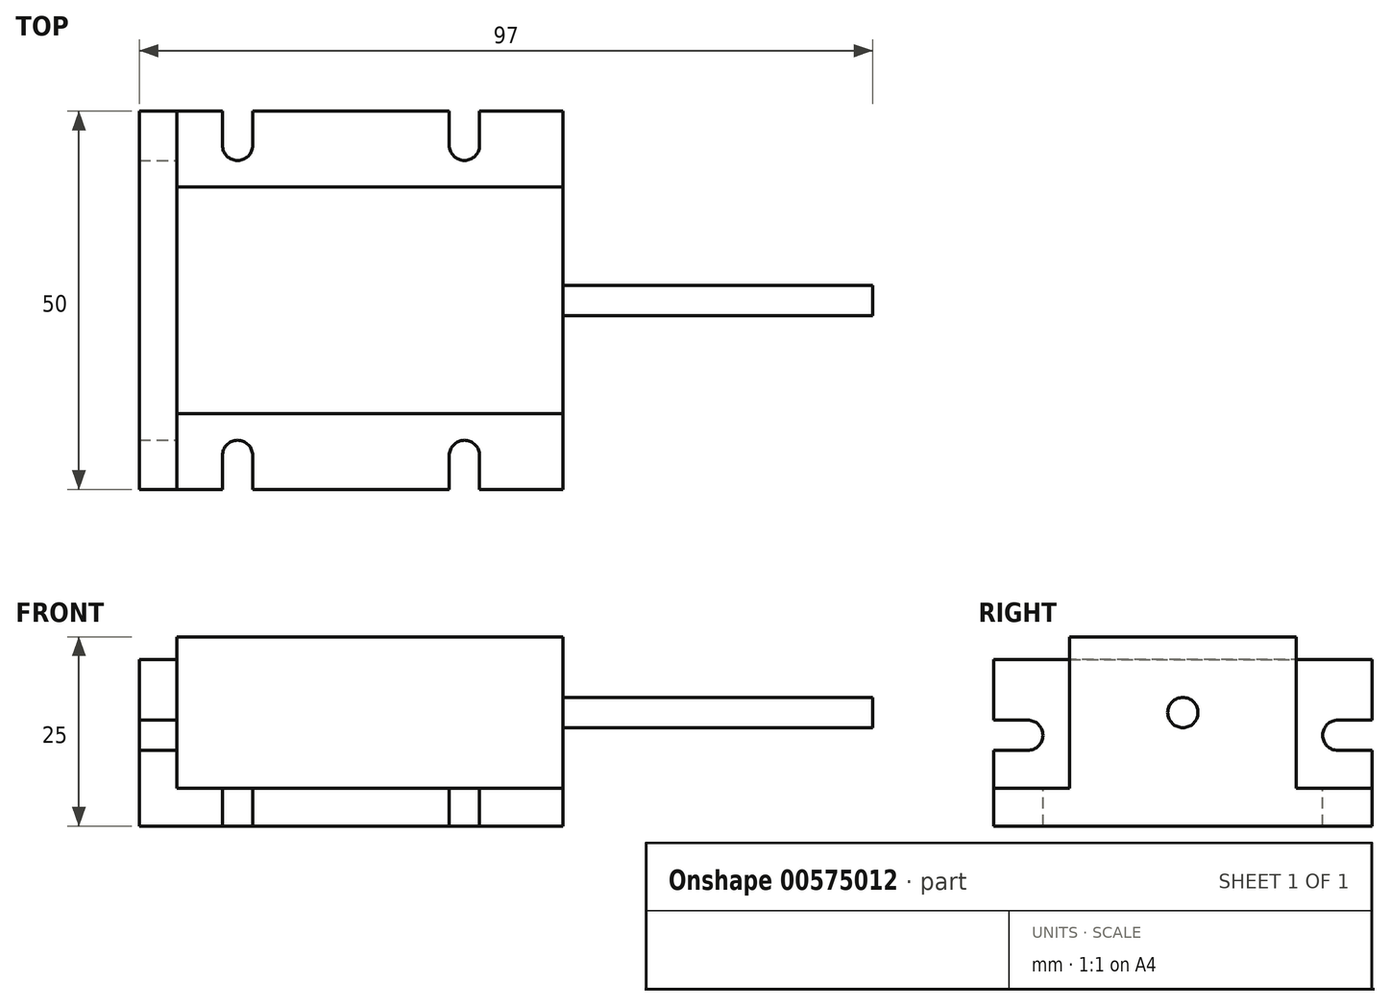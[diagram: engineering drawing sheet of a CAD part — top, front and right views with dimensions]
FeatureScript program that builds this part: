
annotation { "Feature Type Name" : "Feature", "Feature Type Description" : "" }
export const myFeature = defineFeature(function(context is Context, id is Id, definition is map)
    precondition{}
    {
        {
            var Q0;
            Q0=qCreatedBy(makeId("Top.planeOp"),FACE);
            var sketch = newSketch(context, id + "F0", { "sketchPlane" : qUnion([Q0])});
            skLineSegment(sketch, "E0.bottom", {"start": v(-28, 25) * mm, "end": v(28, 25) * mm});
            skLineSegment(sketch, "E0.top", {"start": v(-28, -25) * mm, "end": v(28, -25) * mm});
            skLineSegment(sketch, "E0.left", {"start": v(-28, 25) * mm, "end": v(-28, -25) * mm});
            skLineSegment(sketch, "E0.right", {"start": v(28, 25) * mm, "end": v(28, -25) * mm});
            skPoint(sketch, "E0.middle", {"position": v(0, 0) * mm});
            skSolve(sketch);
        }
        {
            var Q0;
            Q0 = qSketchRegion(id + "F0", true);
            extrude(context, id + "F1", {"entities" : qUnion([Q0]), "depth" : 5 * mm, "offsetDistance" : 25 * mm});
        }
        {
            var Q0;
            Q0=makeQuery(id+"F1.opExtrude","CAP_FACE",FACE,{"disambiguationData":[OSD([sQuery(id+"F0.wireOp",EDGE,"E0.bottom"),sQuery(id+"F0.wireOp",EDGE,"E0.top"),sQuery(id+"F0.wireOp",EDGE,"E0.left"),sQuery(id+"F0.wireOp",EDGE,"E0.right")])],"isStart":false});
            var sketch = newSketch(context, id + "F2", { "sketchPlane" : qUnion([Q0])});
            skArc(sketch, "E1", {"start": v(17, -20.5) * mm, "mid": v(15, -18.5) * mm, "end": v(13, -20.5) * mm});
            skPoint(sketch, "E2", {"position": v(15, -18.5) * mm});
            skPoint(sketch, "E3", {"position": v(17, -20.5) * mm});
            skLineSegment(sketch, "E4", {"start": v(17, -20.5) * mm, "end": v(17, -25) * mm});
            skLineSegment(sketch, "E5", {"start": v(13, -20.5) * mm, "end": v(13, -25) * mm});
            skLineSegment(sketch, "E6", {"start": v(13, -25) * mm, "end": v(17, -25) * mm});
            skPoint(sketch, "E7.MirrorP", {"position": v(17, 20.5) * mm});
            skArc(sketch, "E8.MirrorCS", {"start": v(17, 20.5) * mm, "mid": v(15, 18.5) * mm, "end": v(13, 20.5) * mm});
            skLineSegment(sketch, "E9.MirrorCS", {"start": v(13, 25) * mm, "end": v(17, 25) * mm});
            skLineSegment(sketch, "E10.MirrorCS", {"start": v(17, 20.5) * mm, "end": v(17, 25) * mm});
            skPoint(sketch, "E11.MirrorP", {"position": v(15, 18.5) * mm});
            skLineSegment(sketch, "E12.MirrorCS", {"start": v(13, 20.5) * mm, "end": v(13, 25) * mm});
            skArc(sketch, "E13.MirrorCS", {"start": v(-17, 20.5) * mm, "mid": v(-15, 18.5) * mm, "end": v(-13, 20.5) * mm});
            skArc(sketch, "E14.MirrorCS", {"start": v(-17, -20.5) * mm, "mid": v(-15, -18.5) * mm, "end": v(-13, -20.5) * mm});
            skLineSegment(sketch, "E15.MirrorCS", {"start": v(-13, 25) * mm, "end": v(-17, 25) * mm});
            skPoint(sketch, "E16.MirrorP", {"position": v(-17, 20.5) * mm});
            skPoint(sketch, "E17.MirrorP", {"position": v(-15, 18.5) * mm});
            skPoint(sketch, "E18.MirrorP", {"position": v(-17, -20.5) * mm});
            skLineSegment(sketch, "E19.MirrorCS", {"start": v(-13, -25) * mm, "end": v(-17, -25) * mm});
            skPoint(sketch, "E20.MirrorP", {"position": v(-15, -18.5) * mm});
            skLineSegment(sketch, "E21.MirrorCS", {"start": v(-17, 20.5) * mm, "end": v(-17, 25) * mm});
            skLineSegment(sketch, "E22.MirrorCS", {"start": v(-13, 20.5) * mm, "end": v(-13, 25) * mm});
            skLineSegment(sketch, "E23.MirrorCS", {"start": v(-13, -20.5) * mm, "end": v(-13, -25) * mm});
            skLineSegment(sketch, "E24.MirrorCS", {"start": v(-17, -20.5) * mm, "end": v(-17, -25) * mm});
            skSolve(sketch);
        }
        {
            var Q0;
            Q0 = qSketchRegion(id + "F2", true);
            extrude(context, id + "F3", {"entities" : qUnion([Q0]), "operationType" : NewBodyOperationType.REMOVE, "endBound" : BoundingType.UP_TO_NEXT, "oppositeDirection" : true, "depth" : 25 * mm, "offsetDistance" : 25 * mm});
        }
        {
            var Q0;
            Q0=makeQuery(id+"F1.opExtrude","CAP_FACE",FACE,{"disambiguationData":[OSD([sQuery(id+"F0.wireOp",EDGE,"E0.bottom"),sQuery(id+"F0.wireOp",EDGE,"E0.top"),sQuery(id+"F0.wireOp",EDGE,"E0.left"),sQuery(id+"F0.wireOp",EDGE,"E0.right")])],"isStart":false});
            var sketch = newSketch(context, id + "F4", { "sketchPlane" : qUnion([Q0])});
            skLineSegment(sketch, "E25", {"start": v(-23, -25) * mm, "end": v(-23, 25) * mm});
            skLineSegment(sketch, "E26", {"start": v(-23, 25) * mm, "end": v(-28, 25) * mm});
            skLineSegment(sketch, "E27", {"start": v(-28, 25) * mm, "end": v(-28, -25) * mm});
            skLineSegment(sketch, "E28", {"start": v(-28, -25) * mm, "end": v(-23, -25) * mm});
            skSolve(sketch);
        }
        {
            var Q0;
            Q0 = qSketchRegion(id + "F4", true);
            extrude(context, id + "F5", {"entities" : qUnion([Q0]), "operationType" : NewBodyOperationType.ADD, "depth" : (22 - 5) * mm, "offsetDistance" : 25 * mm});
        }
        {
            var Q0;
            Q0=makeQuery(id+"F1.opExtrude","CAP_FACE",FACE,{"disambiguationData":[OSD([sQuery(id+"F0.wireOp",EDGE,"E0.bottom"),sQuery(id+"F0.wireOp",EDGE,"E0.top"),sQuery(id+"F0.wireOp",EDGE,"E0.left"),sQuery(id+"F0.wireOp",EDGE,"E0.right")])],"isStart":false});
            var sketch = newSketch(context, id + "F6", { "sketchPlane" : qUnion([Q0])});
            skLineSegment(sketch, "E29.bottom", {"start": v(-23, 15) * mm, "end": v(28, 15) * mm});
            skLineSegment(sketch, "E29.top", {"start": v(-23, -15) * mm, "end": v(28, -15) * mm});
            skLineSegment(sketch, "E29.left", {"start": v(-23, 15) * mm, "end": v(-23, -15) * mm});
            skLineSegment(sketch, "E29.right", {"start": v(28, 15) * mm, "end": v(28, -15) * mm});
            skPoint(sketch, "E29.middle", {"position": v(2.5, 0) * mm});
            skSolve(sketch);
        }
        {
            var Q0;
            Q0 = qSketchRegion(id + "F6", true);
            extrude(context, id + "F7", {"entities" : qUnion([Q0]), "operationType" : NewBodyOperationType.ADD, "depth" : (25 - 5) * mm, "offsetDistance" : 25 * mm});
        }
        {
            var Q0;
            {var subQ1=sQuery(id+"F4.wireOp",EDGE,"E25");var subQ2=sQuery(id+"F0.wireOp",EDGE,"E0.top");Q0=makeQuery(id+"F7.boolean.opBoolean","SPLIT",FACE,{"disambiguationData":[TD([makeQuery(id+"F1.opExtrude","SWEPT_FACE",FACE,{"disambiguationData":[OSD([subQ2])]})])],"derivedFrom":makeQuery(id+"F5.opExtrude","SWEPT_FACE",FACE,{"disambiguationData":[OSD([subQ1])]})});}
            var sketch = newSketch(context, id + "F8", { "sketchPlane" : qUnion([Q0])});
            skArc(sketch, "E30", {"start": v(-20.5, 10) * mm, "mid": v(-18.5, 12) * mm, "end": v(-20.5, 14) * mm});
            skPoint(sketch, "E31", {"position": v(-20.5, 10) * mm});
            skPoint(sketch, "E32", {"position": v(-18.5, 12) * mm});
            skLineSegment(sketch, "E33", {"start": v(-20.5, 10) * mm, "end": v(-25, 10) * mm});
            skLineSegment(sketch, "E34", {"start": v(-20.5, 14) * mm, "end": v(-25, 14) * mm});
            skLineSegment(sketch, "E35", {"start": v(-25, 14) * mm, "end": v(-25, 10) * mm});
            skArc(sketch, "E36.MirrorCS", {"start": v(20.5, 10) * mm, "mid": v(18.5, 12) * mm, "end": v(20.5, 14) * mm});
            skPoint(sketch, "E37.MirrorP", {"position": v(18.5, 12) * mm});
            skPoint(sketch, "E38.MirrorP", {"position": v(20.5, 10) * mm});
            skLineSegment(sketch, "E39.MirrorCS", {"start": v(25, 14) * mm, "end": v(25, 10) * mm});
            skLineSegment(sketch, "E40.MirrorCS", {"start": v(20.5, 10) * mm, "end": v(25, 10) * mm});
            skLineSegment(sketch, "E41.MirrorCS", {"start": v(20.5, 14) * mm, "end": v(25, 14) * mm});
            skSolve(sketch);
        }
        {
            var Q0;
            Q0 = qSketchRegion(id + "F8", true);
            extrude(context, id + "F9", {"entities" : qUnion([Q0]), "operationType" : NewBodyOperationType.REMOVE, "endBound" : BoundingType.UP_TO_NEXT, "oppositeDirection" : true, "depth" : 25 * mm, "offsetDistance" : 25 * mm});
        }
        {
            var Q0;
            Q0=makeQuery(id+"F7.boolean.opBoolean","MERGE",FACE,{"derivedFrom":[makeQuery(id+"F1.opExtrude","SWEPT_FACE",FACE,{"disambiguationData":[OSD([sQuery(id+"F0.wireOp",EDGE,"E0.right")])]}),makeQuery(id+"F7.opExtrude","SWEPT_FACE",FACE,{"disambiguationData":[OSD([sQuery(id+"F6.wireOp",EDGE,"E29.right")])]})]});
            var sketch = newSketch(context, id + "F10", { "sketchPlane" : qUnion([Q0])});
            skCircle(sketch, "E42", {"center": v(0, 15) * mm, "radius": 2 * mm});
            skPoint(sketch, "E42.centerSnap0", {"position": v(-15, 15) * mm});
            skSolve(sketch);
        }
        {
            var Q0;
            Q0 = qSketchRegion(id + "F10", true);
            extrude(context, id + "F11", {"entities" : qUnion([Q0]), "operationType" : NewBodyOperationType.ADD, "depth" : 41 * mm, "offsetDistance" : 25 * mm});
        }
    });
